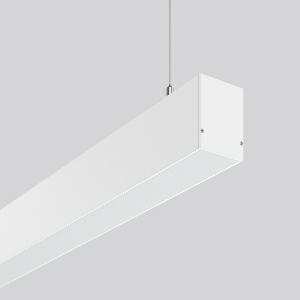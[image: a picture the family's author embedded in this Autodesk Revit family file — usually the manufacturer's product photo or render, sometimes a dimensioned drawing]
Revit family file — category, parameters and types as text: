
# Revit family: less_is_more_50_312314_002_1_76_0d53
name_source: partatom
category: Lighting Fixtures
units: mm (PartAtom-declared; Revit-internal decimal feet)

## family parameters
Cut with Voids When Loaded = No
Host = Face
Light Source = No
Part Type = Normal
Room Calculation Point = No
Round Connector Dimension = Use Diameter
Shared = No

## types (1)
- LESS IS MORE 50 (1 x LED Modul 840, 4850 lm, 4000)
    Apparent Load = 40 VA
    CIE Flux Codes = 48 79 95 100 100
    Color Rendering = 80
    Color Temperature = 4000
    Default Elevation = 1800 mm
    Description = Series: LESS IS MORE 50
Linear pendant luminaire for aesthetically sophisticated lighting. Housing: extruded aluminium profile, powder-coated. End cap aluminium powder-coated. Canopy made of aluminium, powder-coated. Diffuser made of non-yellowing plastic (PMMA), opal. Direct light emission. Suitable for pendant. 2-point steel cable suspension freely positionable and infinitely height-adjustable. Special lengths available on request. LED unit with integrated converter interchangeable and removable. Suitable for through-wiring. With sensors or as a safety luminaire on request. 
Colour: traffic white, matt (RAL 9016)
Length: 1687 mm
Width: 57 mm
Height: 75 mm
Suspension length: 2000 mm
Lamp: LED
Socket: without socket
Colour temperature: 4000K
Colour rendering index (CRI): 80
System power: 40 W
Rated luminous flux: 4850 lm
Luminous efficiency: 121 lm/W
Control gear: Converter, dimmable, DALI
Protection class: I
Type of protection: IP 20
    Height = 75 mm
    Lamp = 1 x LED Modul 840
    Lamp Light Flux = 4850 lm
    Lamp count = 1
    Length = 1687 mm
    Lifetime = 50000 h
    Luminous efficacy = 121 lm/W
    Manufacturer = RZB
    ModVariant = No
    Model = 312314.002.1.76
    Mounting Place = Ceiling
    Mounting Type = Pendant
    Number of Poles = 1
    OnlyDefault = Yes
    Power Factor = 1
    Product Name = LESS IS MORE 50
    Product group = Pendant LED linear luminaires
    ProductGroupID = 907
    Protection Class = Protection class I
    Protection Degree = IP 20
    RLX_Detail_Level = 1
    RLX_Emergency_Light_Flux = 0 lm
    RLX_Emergency_Type = 0
    RLX_Emergency_Type_DB = No
    RlxData = <blob elided: 20597 chars, md5=b3a939a2>
    Socket = socket
    Standby Power = 0 W
    System Light Flux = 4850 lm
    System Power = 40 W
    Type Comments = Product without accessories
    Type Image = 312318.002.jpg
    URL = http://relux.com
    VarID = ---
    Voltage = 230 V
    Voltage Range = 220-240 V
    Weight = 0.00 kg
    Width = 57 mm

## geometry (parser evidence)
native form markers: Blend x4, Sweep x12
no freeform markers — native parametric forms only
